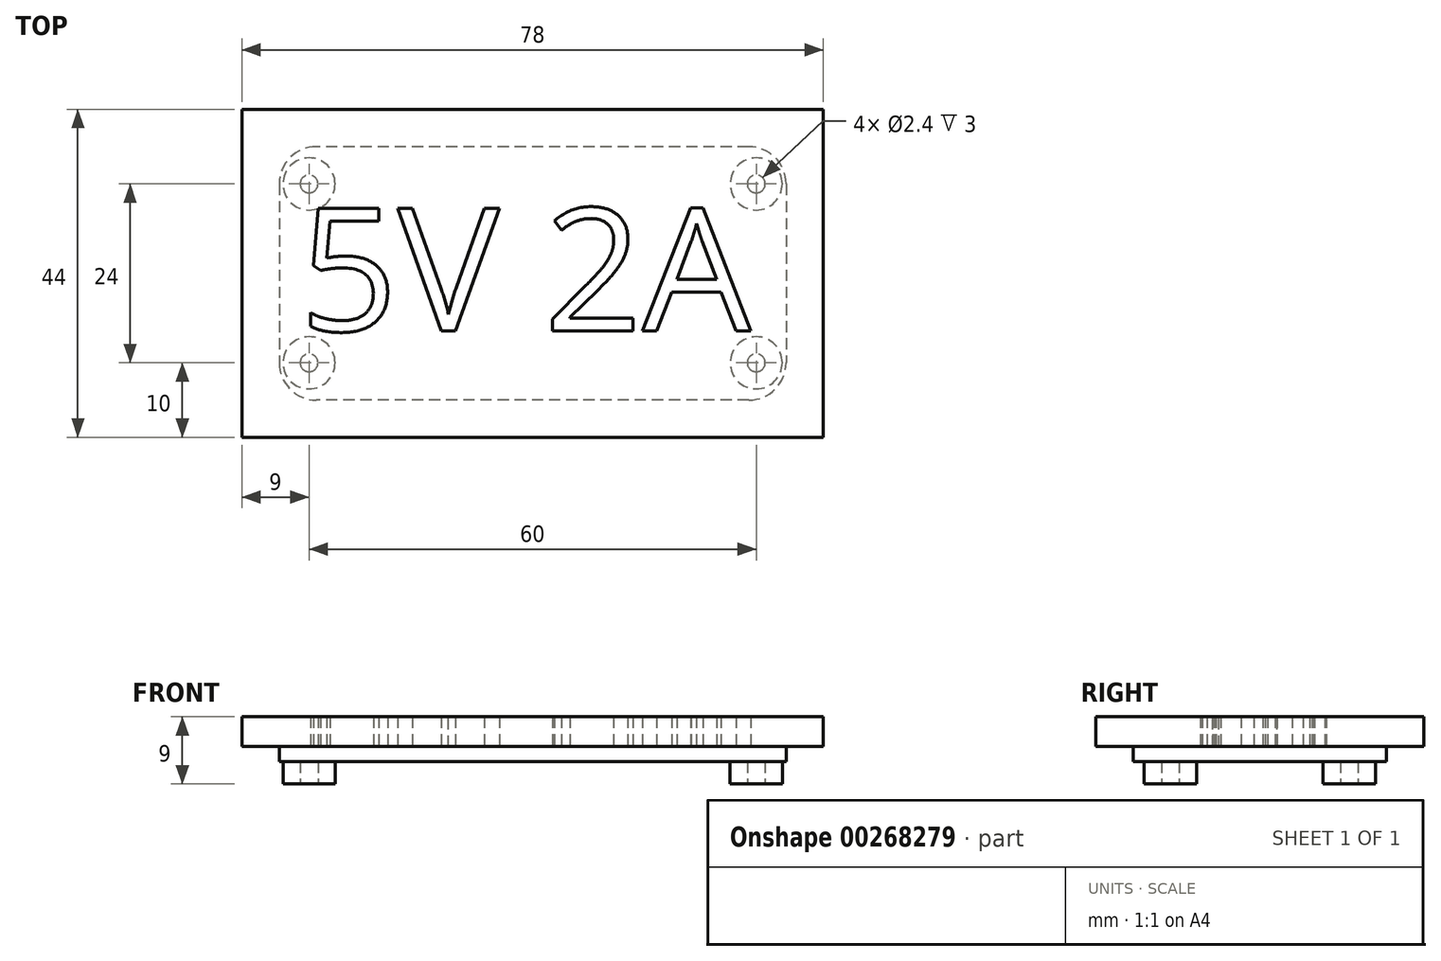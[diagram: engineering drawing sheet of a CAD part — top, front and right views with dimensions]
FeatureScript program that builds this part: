
annotation { "Feature Type Name" : "Feature", "Feature Type Description" : "" }
export const myFeature = defineFeature(function(context is Context, id is Id, definition is map)
    precondition{}
    {
        {
            var Q0;
            Q0=qCreatedBy(makeId("Top.planeOp"),FACE);
            var sketch = newSketch(context, id + "F0", { "sketchPlane" : qUnion([Q0])});
            skLineSegment(sketch, "E0.bottom", {"start": v(34, 17) * mm, "end": v(-34, 17) * mm});
            skLineSegment(sketch, "E0.top", {"start": v(34, -17) * mm, "end": v(-34, -17) * mm});
            skLineSegment(sketch, "E0.left", {"start": v(34, 17) * mm, "end": v(34, -17) * mm});
            skLineSegment(sketch, "E0.right", {"start": v(-34, 17) * mm, "end": v(-34, -17) * mm});
            skPoint(sketch, "E0.middle", {"position": v(0, 0) * mm});
            skLineSegment(sketch, "E1.bottom", {"start": v(30, 12) * mm, "end": v(-30, 12) * mm, "construction": true});
            skLineSegment(sketch, "E1.top", {"start": v(30, -12) * mm, "end": v(-30, -12) * mm, "construction": true});
            skLineSegment(sketch, "E1.left", {"start": v(30, 12) * mm, "end": v(30, -12) * mm, "construction": true});
            skLineSegment(sketch, "E1.right", {"start": v(-30, 12) * mm, "end": v(-30, -12) * mm, "construction": true});
            skSolve(sketch);
        }
        {
            var Q0;
            Q0=makeQuery(id+"F0.imprint","IMPRINT",FACE,{"disambiguationData":[TD([[makeQuery(id+"F0.imprint","IMPRINT",EDGE,{"derivedFrom":sQuery(id+"F0.wireOp",EDGE,"E0.bottom")}),1.0]])]});
            extrude(context, id + "F1", {"entities" : qUnion([Q0]), "depth" : 2 * mm});
        }
        {
            var Q0;
            Q0=makeQuery(id+"F0.imprint","IMPRINT",FACE,{"disambiguationData":[TD([[makeQuery(id+"F0.imprint","IMPRINT",EDGE,{"derivedFrom":sQuery(id+"F0.wireOp",EDGE,"E0.bottom")}),1.0]])]});
            var sketch = newSketch(context, id + "F2", { "sketchPlane" : qUnion([Q0])});
            skCircle(sketch, "E2", {"center": v(-30, 12) * mm, "radius": 3.5 * mm});
            skCircle(sketch, "E3", {"center": v(30, 12) * mm, "radius": 3.5 * mm});
            skCircle(sketch, "E4", {"center": v(30, -12) * mm, "radius": 3.5 * mm});
            skCircle(sketch, "E5", {"center": v(-30, -12) * mm, "radius": 3.5 * mm});
            skSolve(sketch);
        }
        {
            var Q0;
            Q0=makeQuery(id+"F2.imprint","IMPRINT",FACE,{"disambiguationData":[TD([[makeQuery(id+"F2.imprint","IMPRINT",EDGE,{"derivedFrom":sQuery(id+"F2.wireOp",EDGE,"E4")}),1.0]])]});
            var Q1;
            Q1=makeQuery(id+"F2.imprint","IMPRINT",FACE,{"disambiguationData":[TD([[makeQuery(id+"F2.imprint","IMPRINT",EDGE,{"derivedFrom":sQuery(id+"F2.wireOp",EDGE,"E5")}),1.0]])]});
            var Q2;
            Q2=makeQuery(id+"F2.imprint","IMPRINT",FACE,{"disambiguationData":[TD([[makeQuery(id+"F2.imprint","IMPRINT",EDGE,{"derivedFrom":sQuery(id+"F2.wireOp",EDGE,"E3")}),1.0]])]});
            var Q3;
            Q3=makeQuery(id+"F2.imprint","IMPRINT",FACE,{"disambiguationData":[TD([[makeQuery(id+"F2.imprint","IMPRINT",EDGE,{"derivedFrom":sQuery(id+"F2.wireOp",EDGE,"E2")}),1.0]])]});
            extrude(context, id + "F3", {"entities" : qUnion([Q0, Q1, Q2, Q3]), "operationType" : NewBodyOperationType.ADD, "oppositeDirection" : true, "depth" : 3 * mm});
        }
        {
            var Q0;
            Q0=sQuery(id+"F0.wireOp",VERTEX,"E1.right.start");
            var Q1;
            Q1=sQuery(id+"F0.wireOp",VERTEX,"E1.right.end");
            var Q2;
            Q2=sQuery(id+"F0.wireOp",VERTEX,"E1.left.start");
            var Q3;
            Q3=sQuery(id+"F0.wireOp",VERTEX,"E1.left.end");
            var Q4;
            Q4=makeQuery(id+"F1.opExtrude","SWEPT_BODY",BODY,{"disambiguationData":[OSD([sQuery(id+"F0.wireOp",EDGE,"E0.bottom"),sQuery(id+"F0.wireOp",EDGE,"E0.top"),sQuery(id+"F0.wireOp",EDGE,"E0.left"),sQuery(id+"F0.wireOp",EDGE,"E0.right")])]});
            hole(context, id + "F4", {"style" : HoleStyle.SIMPLE, "endStyle" : HoleEndStyle.THROUGH, "standardTappedOrClearance" : lookupTablePath({ "standard" : "ISO", "engagement" : "75%", "pitch" : "0.6 mm", "size" : "M3", "type" : "Tapped" }), "standardBlindInLast" : lookupTablePath({ "standard" : "ISO", "engagement" : "75%", "pitch" : "0.6 mm", "size" : "M3", "type" : "Tapped" }), "holeDiameter" : 2.4 * mm, "showTappedDepth" : true, "tappedDepth" : 12 * mm, "tapClearance" : 3, "startFromSketch" : true, "locations" : qUnion([Q0, Q1, Q2, Q3]), "scope" : qUnion([Q4])});
        }
        {
            var Q0;
            Q0=makeQuery(id+"F1.opExtrude","SWEPT_EDGE",EDGE,{"disambiguationData":[OSD([sQuery(id+"F0.wireOp",EDGE,"E0.bottom"),sQuery(id+"F0.wireOp",EDGE,"E0.right")])]});
            var Q1;
            Q1=makeQuery(id+"F1.opExtrude","SWEPT_EDGE",EDGE,{"disambiguationData":[OSD([sQuery(id+"F0.wireOp",EDGE,"E0.bottom"),sQuery(id+"F0.wireOp",EDGE,"E0.left")])]});
            var Q2;
            Q2=makeQuery(id+"F1.opExtrude","SWEPT_EDGE",EDGE,{"disambiguationData":[OSD([sQuery(id+"F0.wireOp",EDGE,"E0.top"),sQuery(id+"F0.wireOp",EDGE,"E0.left")])]});
            var Q3;
            Q3=makeQuery(id+"F1.opExtrude","SWEPT_EDGE",EDGE,{"disambiguationData":[OSD([sQuery(id+"F0.wireOp",EDGE,"E0.top"),sQuery(id+"F0.wireOp",EDGE,"E0.right")])]});
            fillet(context, id + "F5", {"entities" : qUnion([Q0, Q1, Q2, Q3]), "radius" : 5 * mm, "tangentPropagation" : true, "allowEdgeOverflow" : false});
        }
        {
            var Q0;
            {var subQ1=sQuery(id+"F0.wireOp",EDGE,"E0.left");var subQ6=sQuery(id+"F0.wireOp",EDGE,"E0.right");var subQ7=sQuery(id+"F0.wireOp",EDGE,"E0.bottom");var subQ8=sQuery(id+"F0.wireOp",EDGE,"E0.top");Q0=makeQuery(id+"Fy1oZVBtFrOcqaw_1.boolean.opBoolean","SPLIT",FACE,{"disambiguationData":[TD([makeQuery(id+"F1.opExtrude","SWEPT_FACE",FACE,{"disambiguationData":[OSD([subQ7])]})])],"derivedFrom":makeQuery(id+"F1.opExtrude","CAP_FACE",FACE,{"disambiguationData":[OSD([subQ7,subQ8,subQ1,subQ6])],"isStart":false})});}
            var sketch = newSketch(context, id + "F6", { "sketchPlane" : qUnion([Q0])});
            skLineSegment(sketch, "E6.0", {"start": v(39, 22) * mm, "end": v(-39, 22) * mm});
            skLineSegment(sketch, "E6.1", {"start": v(39, 22) * mm, "end": v(39, -22) * mm});
            skLineSegment(sketch, "E6.2", {"start": v(39, -22) * mm, "end": v(-39, -22) * mm});
            skLineSegment(sketch, "E6.3", {"start": v(-39, 22) * mm, "end": v(-39, -22) * mm});
            skText(sketch, "E7", { "text": "5V 2A\n", "fontName": "OpenSans-Regular.ttf"});
            const initialGuessF6  = {"E7": [-0.0313, -0.00772, 1, 0, 0.01658]};
            skSetInitialGuess(sketch, initialGuessF6);
            skSolve(sketch);
        }
        {
            var Q0;
            Q0 = qSketchRegion(id + "F6", true);
            var Q1;
            Q1=makeQuery(id+"F6.imprint","IMPRINT",FACE,{"disambiguationData":[TD([[makeQuery(id+"F6.imprint","IMPRINT",EDGE,{"derivedFrom":sQuery(id+"F6.wireOp",EDGE,"E7.sketch_text.stroke-56")}),1.0]])]});
            extrude(context, id + "F7", {"entities" : qUnion([Q0, Q1]), "operationType" : NewBodyOperationType.ADD, "depth" : 4 * mm});
        }
    });
